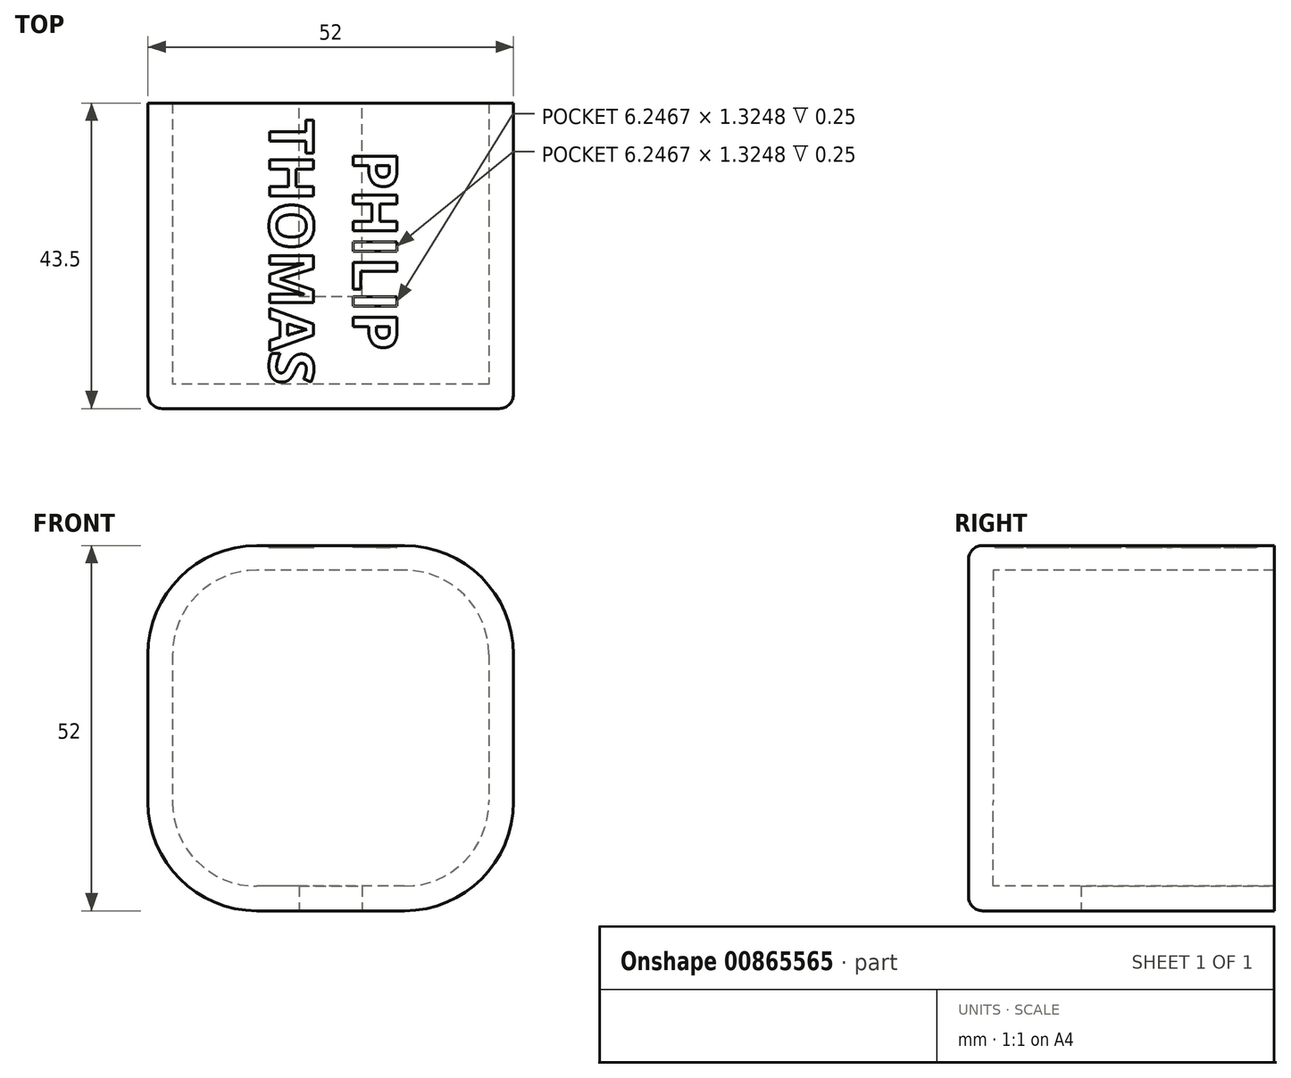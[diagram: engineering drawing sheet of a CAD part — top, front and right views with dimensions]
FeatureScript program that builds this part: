
annotation { "Feature Type Name" : "Feature", "Feature Type Description" : "" }
export const myFeature = defineFeature(function(context is Context, id is Id, definition is map)
    precondition{}
    {
        {
            var Q0;
            Q0=qCreatedBy(makeId("Front.planeOp"),FACE);
            var sketch = newSketch(context, id + "F0", { "sketchPlane" : qUnion([Q0])});
            skLineSegment(sketch, "E0.bottom", {"start": v(22.5, 22.5) * mm, "end": v(-22.5, 22.5) * mm});
            skLineSegment(sketch, "E0.top", {"start": v(22.5, -22.5) * mm, "end": v(-22.5, -22.5) * mm});
            skLineSegment(sketch, "E0.left", {"start": v(22.5, 22.5) * mm, "end": v(22.5, -22.5) * mm});
            skLineSegment(sketch, "E0.right", {"start": v(-22.5, 22.5) * mm, "end": v(-22.5, -22.5) * mm});
            skPoint(sketch, "E0.middle", {"position": v(0, 0) * mm});
            skSolve(sketch);
        }
        {
            var Q0;
            Q0 = qSketchRegion(id + "F0", true);
            extrude(context, id + "F1", {"entities" : qUnion([Q0]), "oppositeDirection" : true, "depth" : 40 * mm, "offsetDistance" : 25 * mm});
        }
        {
            var Q0;
            Q0=makeQuery(id+"F1.opExtrude","SWEPT_EDGE",EDGE,{"disambiguationData":[OSD([sQuery(id+"F0.wireOp",EDGE,"E0.bottom"),sQuery(id+"F0.wireOp",EDGE,"E0.left")])]});
            var Q1;
            Q1=makeQuery(id+"F1.opExtrude","SWEPT_EDGE",EDGE,{"disambiguationData":[OSD([sQuery(id+"F0.wireOp",EDGE,"E0.bottom"),sQuery(id+"F0.wireOp",EDGE,"E0.right")])]});
            var Q2;
            Q2=makeQuery(id+"F1.opExtrude","SWEPT_EDGE",EDGE,{"disambiguationData":[OSD([sQuery(id+"F0.wireOp",EDGE,"E0.top"),sQuery(id+"F0.wireOp",EDGE,"E0.left")])]});
            var Q3;
            Q3=makeQuery(id+"F1.opExtrude","SWEPT_EDGE",EDGE,{"disambiguationData":[OSD([sQuery(id+"F0.wireOp",EDGE,"E0.top"),sQuery(id+"F0.wireOp",EDGE,"E0.right")])]});
            fillet(context, id + "F2", {"entities" : qUnion([Q0, Q1, Q2, Q3]), "radius" : 12 * mm, "tangentPropagation" : true, "allowEdgeOverflow" : false});
        }
        {
            var Q0;
            Q0=makeQuery(id+"F1.opExtrude","CAP_FACE",FACE,{"disambiguationData":[OSD([sQuery(id+"F0.wireOp",EDGE,"E0.bottom"),sQuery(id+"F0.wireOp",EDGE,"E0.top"),sQuery(id+"F0.wireOp",EDGE,"E0.left"),sQuery(id+"F0.wireOp",EDGE,"E0.right")])],"isStart":false});
            shell(context, id + "F3", {"entities" : qUnion([Q0]), "thickness" : 3.5 * mm, "oppositeDirection" : true});
        }
        {
            var Q0;
            Q0=makeQuery(id+"F1.opExtrude","CAP_FACE",FACE,{"disambiguationData":[OSD([sQuery(id+"F0.wireOp",EDGE,"E0.bottom"),sQuery(id+"F0.wireOp",EDGE,"E0.top"),sQuery(id+"F0.wireOp",EDGE,"E0.left"),sQuery(id+"F0.wireOp",EDGE,"E0.right")])],"isStart":false});
            var sketch = newSketch(context, id + "F4", { "sketchPlane" : qUnion([Q0])});
            skLineSegment(sketch, "E1.bottom", {"start": v(4.5, 8.58) * mm, "end": v(-4.5, 8.58) * mm});
            skLineSegment(sketch, "E1.top", {"start": v(4.5, -39.48) * mm, "end": v(-4.5, -39.48) * mm});
            skLineSegment(sketch, "E1.left", {"start": v(4.5, 8.58) * mm, "end": v(4.5, -39.48) * mm});
            skLineSegment(sketch, "E1.right", {"start": v(-4.5, 8.58) * mm, "end": v(-4.5, -39.48) * mm});
            skPoint(sketch, "E1.middle", {"position": v(0, -15.45) * mm});
            skSolve(sketch);
        }
        {
            var Q0;
            Q0 = qSketchRegion(id + "F4", true);
            var Q1;
            Q1=makeQuery(id+"F1.opExtrude","CAP_FACE",FACE,{"disambiguationData":[OSD([sQuery(id+"F0.wireOp",EDGE,"E0.bottom"),sQuery(id+"F0.wireOp",EDGE,"E0.top"),sQuery(id+"F0.wireOp",EDGE,"E0.left"),sQuery(id+"F0.wireOp",EDGE,"E0.right")])],"isStart":true});
            extrude(context, id + "F5", {"entities" : qUnion([Q0]), "operationType" : NewBodyOperationType.REMOVE, "endBound" : BoundingType.UP_TO_SURFACE, "oppositeDirection" : true, "depth" : 25 * mm, "endBoundEntityFace" : qUnion([Q1]), "hasOffset" : true, "offsetDistance" : 16 * mm});
        }
        {
            var Q0;
            Q0=makeQuery(id+"F1.opExtrude","CAP_FACE",FACE,{"disambiguationData":[OSD([sQuery(id+"F0.wireOp",EDGE,"E0.bottom"),sQuery(id+"F0.wireOp",EDGE,"E0.top"),sQuery(id+"F0.wireOp",EDGE,"E0.left"),sQuery(id+"F0.wireOp",EDGE,"E0.right")])],"isStart":true});
            var Q1;
            Q1=makeQuery(id+"F5.boolean.opBoolean","COPY",EDGE,{"derivedFrom":makeQuery(id+"F5.opExtrude","CAP_EDGE",EDGE,{"disambiguationData":[OSD([sQuery(id+"F4.wireOp",EDGE,"E1.left")])],"isStart":true})});
            var Q2;
            Q2=makeQuery(id+"F5.boolean.opBoolean","COPY",EDGE,{"derivedFrom":makeQuery(id+"F5.opExtrude","CAP_EDGE",EDGE,{"disambiguationData":[OSD([sQuery(id+"F4.wireOp",EDGE,"E1.right")])],"isStart":true})});
            fillet(context, id + "F6", {"entities" : qUnion([Q0, Q1, Q2]), "radius" : 2 * mm, "tangentPropagation" : true, "allowEdgeOverflow" : false});
        }
        {
            var Q0;
            Q0=makeQuery(id+"F1.opExtrude","SWEPT_FACE",FACE,{"disambiguationData":[OSD([sQuery(id+"F0.wireOp",EDGE,"E0.bottom")])]});
            var sketch = newSketch(context, id + "F7", { "sketchPlane" : qUnion([Q0])});
            skText(sketch, "E2", { "text": "  PHILIP \nTHOMAS", "fontName": "OpenSans-Bold.ttf"});
            const initialGuessF7  = {"E2": [0.0032, 0.03775, 0, -1, 0.0063]};
            skSetInitialGuess(sketch, initialGuessF7);
            skSolve(sketch);
        }
        {
            var Q0;
            Q0 = qSketchRegion(id + "F7", true);
            extrude(context, id + "F8", {"entities" : qUnion([Q0]), "operationType" : NewBodyOperationType.REMOVE, "oppositeDirection" : true, "depth" : 0.25 * mm, "offsetDistance" : 25 * mm});
        }
    });
